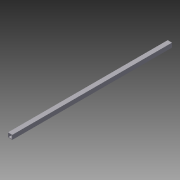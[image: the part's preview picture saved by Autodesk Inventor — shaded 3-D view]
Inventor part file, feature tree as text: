
AUTODESK INVENTOR PART (.ipt)
format: ipt  version: 2012 (Build 160160000, 160)  size: 72,192 bytes
history: native  units: in
note: dims shown in document units (in); Inventor stores cm internally (conversion verified against a paired STEP export)
features: extrude x1, shell x1, sketch x1
ambient origin geometry x8: Origin, YZ Plane, XZ Plane, XY Plane, X Axis, Y Axis, Z Axis, Center Point
bodies: Solid1 (feature_tree)
feature tree (3):
  extrude  "Extrusion1"  Depth=1.0in
  shell  "Shell1"  Thickness=37.0in
  sketch  "Sketch1"  dims[d0=1.0in d1=1.0in d2=37.0in d3=0.0in d4=0.125in]
